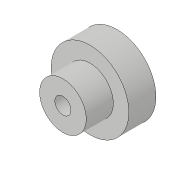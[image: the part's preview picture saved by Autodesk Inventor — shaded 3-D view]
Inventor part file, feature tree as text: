
AUTODESK INVENTOR PART (.ipt)
format: ipt  version: 2018.3 (Build 223284000, 284)  size: 92,160 bytes
history: native  units: in
note: dims shown in document units (in); Inventor stores cm internally (conversion verified against a paired STEP export)
features: extrude x2, sketch x2
ambient origin geometry x8: Origin, YZ Plane, XZ Plane, XY Plane, X Axis, Y Axis, Z Axis, Center Point
bodies: Body1 (feature_tree)
feature tree (4):
  extrude  "Extrusion4"  Depth=0.435in TaperAngle=0.0deg
  extrude  "Extrusion5"  Depth=0.2175in TaperAngle=0.0deg
  sketch  "Sketch4"  dims[d9=0.13in d11=0.435in d12=0.0in]
  sketch  "Sketch5"  dims[d13=0.125in d14=0.2175in d15=0.0in d16=0.374in]
